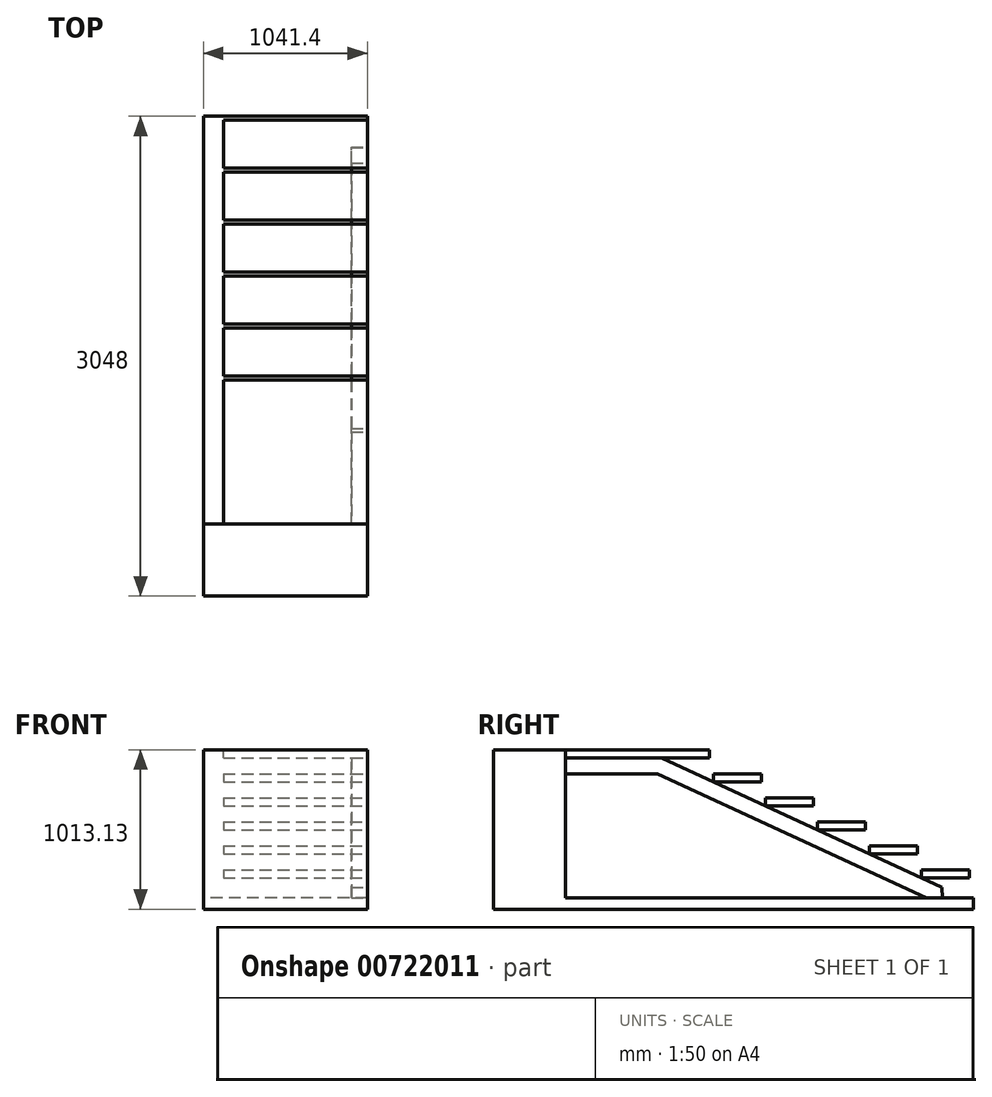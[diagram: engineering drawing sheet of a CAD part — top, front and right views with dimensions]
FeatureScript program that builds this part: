
annotation { "Feature Type Name" : "Feature", "Feature Type Description" : "" }
export const myFeature = defineFeature(function(context is Context, id is Id, definition is map)
    precondition{}
    {
        {
            var Q0;
            Q0=qCreatedBy(makeId("Right.planeOp"),FACE);
            var sketch = newSketch(context, id + "F0", { "sketchPlane" : qUnion([Q0])});
            skLineSegment(sketch, "E0.bottom", {"start": v(0, 0) * mm, "end": v(-457.96, 0) * mm});
            skLineSegment(sketch, "E0.top", {"start": v(0, 939.8) * mm, "end": v(-457.96, 939.8) * mm});
            skLineSegment(sketch, "E0.left", {"start": v(0, 0) * mm, "end": v(0, 939.8) * mm});
            skLineSegment(sketch, "E0.right", {"start": v(-457.96, 0) * mm, "end": v(-457.96, 939.8) * mm});
            skLineSegment(sketch, "E1.bottom", {"start": v(-457.96, 0) * mm, "end": v(2590.04, 0) * mm});
            skLineSegment(sketch, "E1.top", {"start": v(-457.96, -73.33) * mm, "end": v(2590.04, -73.33) * mm});
            skLineSegment(sketch, "E1.left", {"start": v(-457.96, 0) * mm, "end": v(-457.96, -73.33) * mm});
            skLineSegment(sketch, "E1.right", {"start": v(2590.04, 0) * mm, "end": v(2590.04, -73.33) * mm});
            skSolve(sketch);
        }
        {
            var Q0;
            Q0=makeQuery(id+"F0.imprint","IMPRINT",FACE,{"disambiguationData":[TD([[makeQuery(id+"F0.imprint","IMPRINT",EDGE,{"derivedFrom":sQuery(id+"F0.wireOp",EDGE,"E0.top")}),1.0]])]});
            var Q1;
            Q1=makeQuery(id+"F0.imprint","IMPRINT",FACE,{"disambiguationData":[TD([[makeQuery(id+"F0.imprint","IMPRINT",EDGE,{"derivedFrom":sQuery(id+"F0.wireOp",EDGE,"E1.top")}),1.0]])]});
            extrude(context, id + "F1", {"entities" : qUnion([Q0, Q1]), "depth" : 1041.4 * mm, "offsetDistance" : 25.4 * mm});
        }
        {
            var Q0;
            Q0=makeQuery(id+"F1.opExtrude","CAP_FACE",FACE,{"disambiguationData":[OSD([sQuery(id+"F0.wireOp",EDGE,"E0.top"),sQuery(id+"F0.wireOp",EDGE,"E0.left"),sQuery(id+"F0.wireOp",EDGE,"E0.right"),sQuery(id+"F0.wireOp",EDGE,"E1.bottom"),sQuery(id+"F0.wireOp",EDGE,"E1.top"),sQuery(id+"F0.wireOp",EDGE,"E1.left"),sQuery(id+"F0.wireOp",EDGE,"E1.right")])],"isStart":false});
            var sketch = newSketch(context, id + "F2", { "sketchPlane" : qUnion([Q0])});
            skLineSegment(sketch, "E2.bottom", {"start": v(0, 939.8) * mm, "end": v(914.4, 939.8) * mm});
            skLineSegment(sketch, "E2.top", {"start": v(0, 889) * mm, "end": v(914.4, 889) * mm});
            skLineSegment(sketch, "E2.left", {"start": v(0, 939.8) * mm, "end": v(0, 889) * mm});
            skLineSegment(sketch, "E2.right", {"start": v(914.4, 939.8) * mm, "end": v(914.4, 889) * mm});
            skLineSegment(sketch, "E3.bottom", {"start": v(939.8, 787.4) * mm, "end": v(1244.6, 787.4) * mm});
            skLineSegment(sketch, "E3.top", {"start": v(939.8, 736.6) * mm, "end": v(1244.6, 736.6) * mm});
            skLineSegment(sketch, "E3.left", {"start": v(939.8, 787.4) * mm, "end": v(939.8, 736.6) * mm});
            skLineSegment(sketch, "E3.right", {"start": v(1244.6, 787.4) * mm, "end": v(1244.6, 736.6) * mm});
            skLineSegment(sketch, "E4.bottom", {"start": v(1270, 635) * mm, "end": v(1574.8, 635) * mm});
            skLineSegment(sketch, "E4.top", {"start": v(1270, 584.2) * mm, "end": v(1574.8, 584.2) * mm});
            skLineSegment(sketch, "E4.left", {"start": v(1270, 635) * mm, "end": v(1270, 584.2) * mm});
            skLineSegment(sketch, "E4.right", {"start": v(1574.8, 635) * mm, "end": v(1574.8, 584.2) * mm});
            skLineSegment(sketch, "E5.bottom", {"start": v(1600.2, 482.6) * mm, "end": v(1905, 482.6) * mm});
            skLineSegment(sketch, "E5.top", {"start": v(1600.2, 431.8) * mm, "end": v(1905, 431.8) * mm});
            skLineSegment(sketch, "E5.left", {"start": v(1600.2, 482.6) * mm, "end": v(1600.2, 431.8) * mm});
            skLineSegment(sketch, "E5.right", {"start": v(1905, 482.6) * mm, "end": v(1905, 431.8) * mm});
            skLineSegment(sketch, "E6.bottom", {"start": v(1930.4, 330.2) * mm, "end": v(2235.2, 330.2) * mm});
            skLineSegment(sketch, "E6.top", {"start": v(1930.4, 279.4) * mm, "end": v(2235.2, 279.4) * mm});
            skLineSegment(sketch, "E6.left", {"start": v(1930.4, 330.2) * mm, "end": v(1930.4, 279.4) * mm});
            skLineSegment(sketch, "E6.right", {"start": v(2235.2, 330.2) * mm, "end": v(2235.2, 279.4) * mm});
            skLineSegment(sketch, "E7.bottom", {"start": v(2260.6, 177.8) * mm, "end": v(2565.4, 177.8) * mm});
            skLineSegment(sketch, "E7.top", {"start": v(2260.6, 127) * mm, "end": v(2565.4, 127) * mm});
            skLineSegment(sketch, "E7.left", {"start": v(2260.6, 177.8) * mm, "end": v(2260.6, 127) * mm});
            skLineSegment(sketch, "E7.right", {"start": v(2565.4, 177.8) * mm, "end": v(2565.4, 127) * mm});
            skSolve(sketch);
        }
        {
            var Q0;
            Q0=makeQuery(id+"F2.imprint","IMPRINT",FACE,{"disambiguationData":[TD([[makeQuery(id+"F2.imprint","IMPRINT",EDGE,{"derivedFrom":sQuery(id+"F2.wireOp",EDGE,"E2.bottom")}),-1.0]])]});
            var Q1;
            Q1=makeQuery(id+"F2.imprint","IMPRINT",FACE,{"disambiguationData":[TD([[makeQuery(id+"F2.imprint","IMPRINT",EDGE,{"derivedFrom":sQuery(id+"F2.wireOp",EDGE,"E3.bottom")}),-1.0]])]});
            var Q2;
            Q2=makeQuery(id+"F2.imprint","IMPRINT",FACE,{"disambiguationData":[TD([[makeQuery(id+"F2.imprint","IMPRINT",EDGE,{"derivedFrom":sQuery(id+"F2.wireOp",EDGE,"E4.bottom")}),-1.0]])]});
            var Q3;
            Q3=makeQuery(id+"F2.imprint","IMPRINT",FACE,{"disambiguationData":[TD([[makeQuery(id+"F2.imprint","IMPRINT",EDGE,{"derivedFrom":sQuery(id+"F2.wireOp",EDGE,"E5.bottom")}),-1.0]])]});
            var Q4;
            Q4=makeQuery(id+"F2.imprint","IMPRINT",FACE,{"disambiguationData":[TD([[makeQuery(id+"F2.imprint","IMPRINT",EDGE,{"derivedFrom":sQuery(id+"F2.wireOp",EDGE,"E6.bottom")}),-1.0]])]});
            var Q5;
            Q5=makeQuery(id+"F2.imprint","IMPRINT",FACE,{"disambiguationData":[TD([[makeQuery(id+"F2.imprint","IMPRINT",EDGE,{"derivedFrom":sQuery(id+"F2.wireOp",EDGE,"E7.bottom")}),-1.0]])]});
            extrude(context, id + "F3", {"entities" : qUnion([Q0, Q1, Q2, Q3, Q4, Q5]), "oppositeDirection" : true, "depth" : 914.4 * mm, "offsetDistance" : 25.4 * mm});
        }
        {
            var Q0;
            Q0=makeQuery(id+"F1.opExtrude","CAP_FACE",FACE,{"disambiguationData":[OSD([sQuery(id+"F0.wireOp",EDGE,"E0.top"),sQuery(id+"F0.wireOp",EDGE,"E0.left"),sQuery(id+"F0.wireOp",EDGE,"E0.right"),sQuery(id+"F0.wireOp",EDGE,"E1.bottom"),sQuery(id+"F0.wireOp",EDGE,"E1.top"),sQuery(id+"F0.wireOp",EDGE,"E1.left"),sQuery(id+"F0.wireOp",EDGE,"E1.right")])],"isStart":false});
            var sketch = newSketch(context, id + "F4", { "sketchPlane" : qUnion([Q0])});
            skLineSegment(sketch, "E8", {"start": v(608.3, 889) * mm, "end": v(2392.59, 66.13) * mm});
            skLineSegment(sketch, "E9", {"start": v(2293.38, 0) * mm, "end": v(586, 787.4) * mm});
            skLineSegment(sketch, "E10", {"start": v(586, 787.4) * mm, "end": v(608.3, 889) * mm});
            skLineSegment(sketch, "E11", {"start": v(586, 787.4) * mm, "end": v(0, 787.4) * mm});
            skLineSegment(sketch, "E12", {"start": v(0, 787.4) * mm, "end": v(0, 889) * mm});
            skLineSegment(sketch, "E13", {"start": v(0, 889) * mm, "end": v(608.3, 889) * mm});
            skLineSegment(sketch, "E14", {"start": v(2293.38, 0) * mm, "end": v(2394.98, 0) * mm});
            skLineSegment(sketch, "E15", {"start": v(2565.4, 127) * mm, "end": v(2504.05, 127) * mm});
            skLineSegment(sketch, "E16", {"start": v(2504.05, 127) * mm, "end": v(2392.59, 66.13) * mm});
            skLineSegment(sketch, "E17", {"start": v(2392.59, 66.13) * mm, "end": v(2394.98, 0) * mm});
            skSolve(sketch);
        }
        {
            var Q0;
            Q0 = qSketchRegion(id + "F4", true);
            extrude(context, id + "F5", {"entities" : qUnion([Q0]), "oppositeDirection" : true, "depth" : 101.6 * mm, "offsetDistance" : 25.4 * mm});
        }
    });
